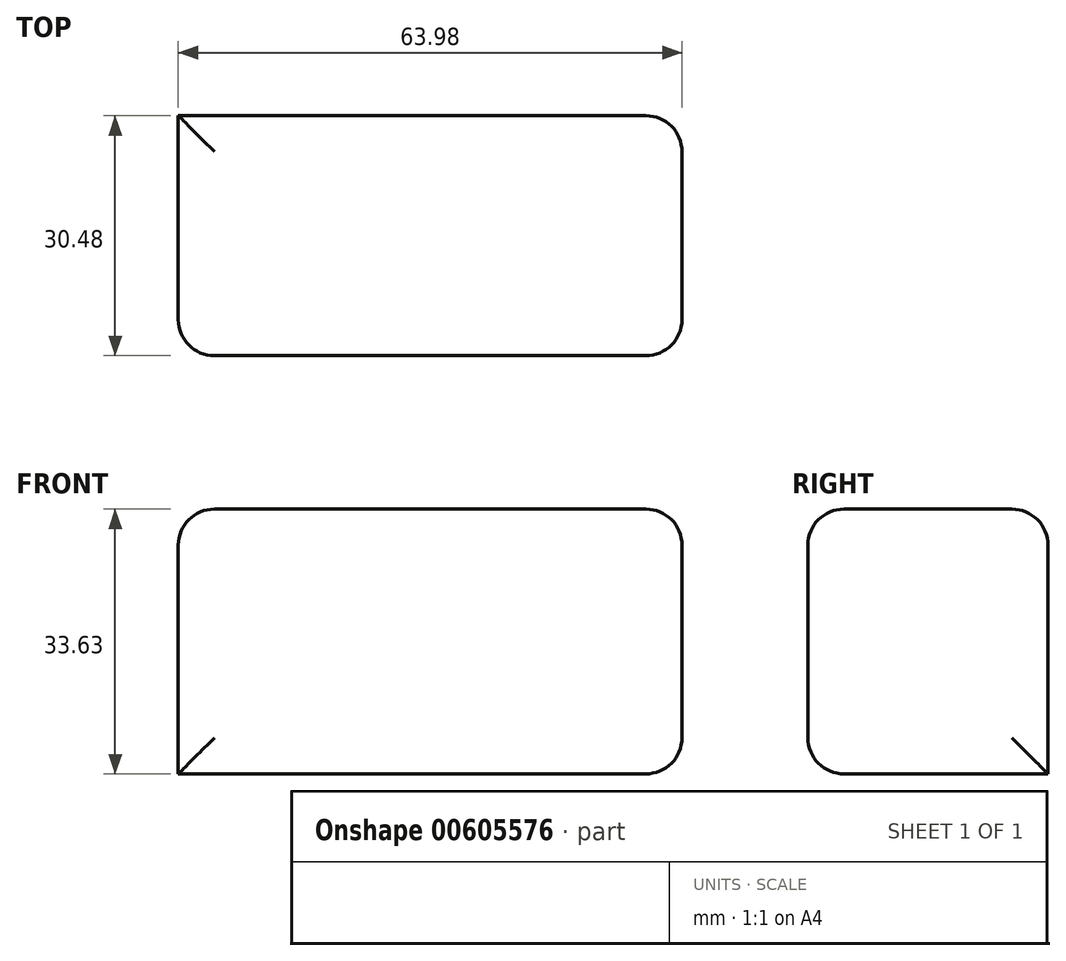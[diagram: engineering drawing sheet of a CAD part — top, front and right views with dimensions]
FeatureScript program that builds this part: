
annotation { "Feature Type Name" : "Feature", "Feature Type Description" : "" }
export const myFeature = defineFeature(function(context is Context, id is Id, definition is map)
    precondition{}
    {
        {
            var Q0;
            Q0=qCreatedBy(makeId("Front.planeOp"),FACE);
            var sketch = newSketch(context, id + "F0", { "sketchPlane" : qUnion([Q0])});
            skLineSegment(sketch, "E0.bottom", {"start": v(-144.27, 46.56) * mm, "end": v(-80.3, 46.56) * mm});
            skLineSegment(sketch, "E0.top", {"start": v(-144.27, 12.93) * mm, "end": v(-80.3, 12.93) * mm});
            skLineSegment(sketch, "E0.left", {"start": v(-144.27, 46.56) * mm, "end": v(-144.27, 12.93) * mm});
            skLineSegment(sketch, "E0.right", {"start": v(-80.3, 46.56) * mm, "end": v(-80.3, 12.93) * mm});
            skSolve(sketch);
        }
        {
            var Q0;
            Q0 = qSketchRegion(id + "F0", true);
            extrude(context, id + "F1", {"entities" : qUnion([Q0]), "depth" : 30.48 * mm, "offsetDistance" : 30.48 * mm});
        }
        {
            var Q0;
            Q0=makeQuery(id+"F1.opExtrude","SWEPT_FACE",FACE,{"disambiguationData":[OSD([sQuery(id+"F0.wireOp",EDGE,"E0.bottom")])]});
            var Q1;
            Q1=makeQuery(id+"F1.opExtrude","CAP_FACE",FACE,{"disambiguationData":[OSD([sQuery(id+"F0.wireOp",EDGE,"E0.bottom"),sQuery(id+"F0.wireOp",EDGE,"E0.top"),sQuery(id+"F0.wireOp",EDGE,"E0.left"),sQuery(id+"F0.wireOp",EDGE,"E0.right")])],"isStart":false});
            var Q2;
            Q2=makeQuery(id+"F1.opExtrude","SWEPT_FACE",FACE,{"disambiguationData":[OSD([sQuery(id+"F0.wireOp",EDGE,"E0.right")])]});
            fillet(context, id + "F2", {"entities" : qUnion([Q0, Q1, Q2]), "radius" : 4.57 * mm, "tangentPropagation" : true, "allowEdgeOverflow" : false});
        }
    });
